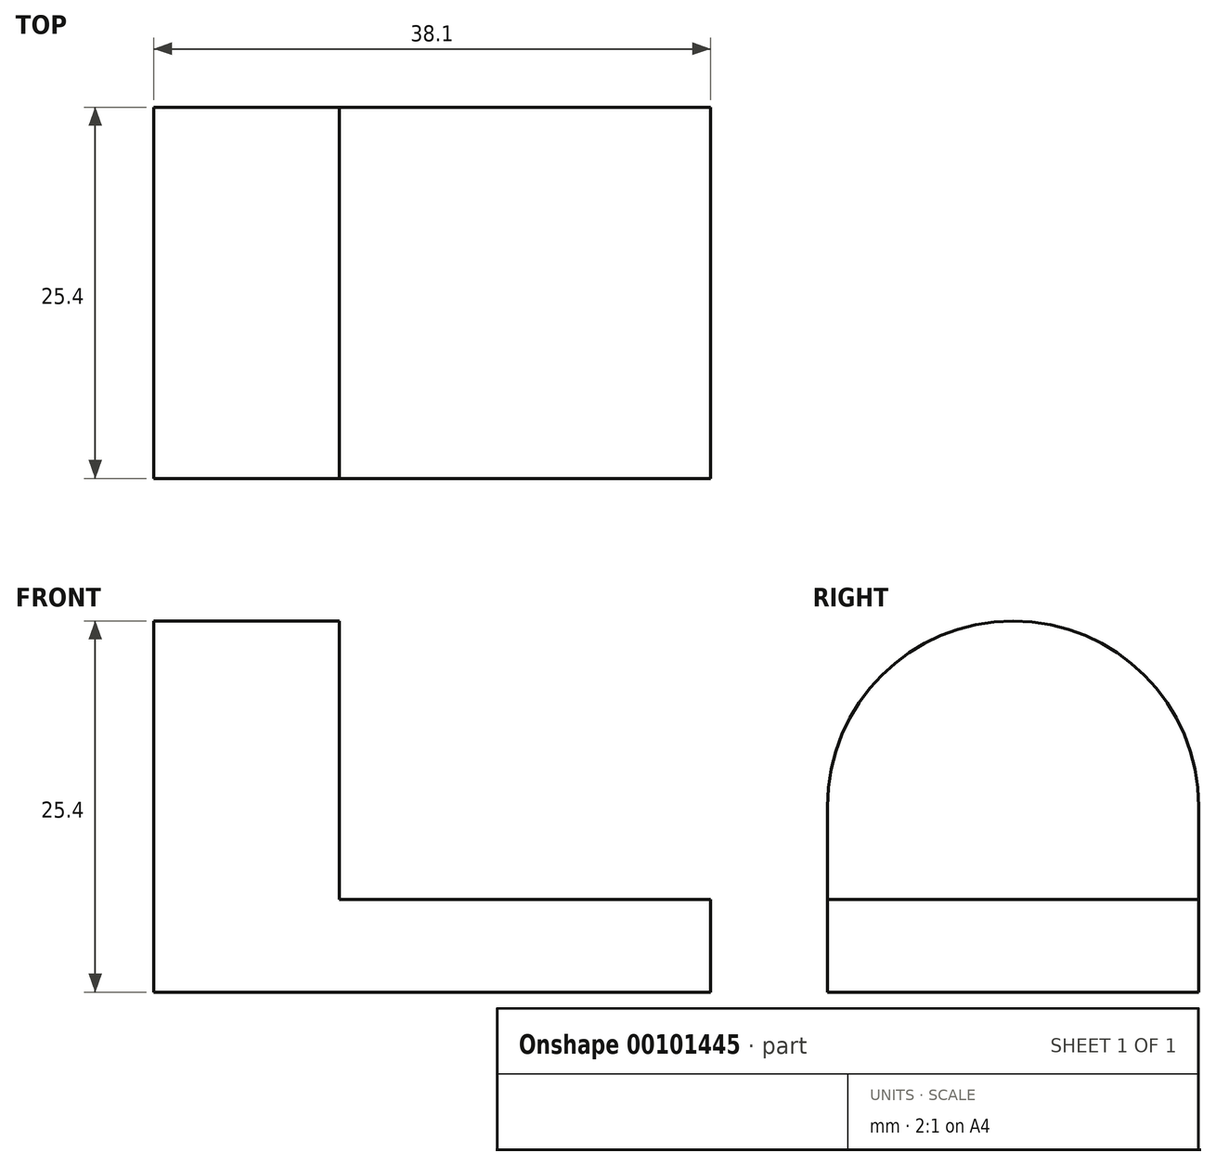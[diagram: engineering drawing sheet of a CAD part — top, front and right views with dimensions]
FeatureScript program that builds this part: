
annotation { "Feature Type Name" : "Feature", "Feature Type Description" : "" }
export const myFeature = defineFeature(function(context is Context, id is Id, definition is map)
    precondition{}
    {
        {
            var Q0;
            Q0=qCreatedBy(makeId("Right.planeOp"),FACE);
            var sketch = newSketch(context, id + "F0", { "sketchPlane" : qUnion([Q0])});
            skLineSegment(sketch, "E0", {"start": v(0, 0) * mm, "end": v(25.4, 0) * mm});
            skLineSegment(sketch, "E1", {"start": v(25.4, 0) * mm, "end": v(25.4, 12.7) * mm});
            skLineSegment(sketch, "E2", {"start": v(0, 0) * mm, "end": v(0, 12.7) * mm});
            skArc(sketch, "E3", {"start": v(25.4, 12.7) * mm, "mid": v(12.7, 25.4) * mm, "end": v(0, 12.7) * mm});
            skSolve(sketch);
        }
        {
            var Q0;
            Q0 = qSketchRegion(id + "F0", true);
            extrude(context, id + "F1", {"entities" : qUnion([Q0]), "depth" : 12.7 * mm});
        }
        {
            var Q0;
            Q0=makeQuery(id+"F1.opExtrude","CAP_FACE",FACE,{"disambiguationData":[OSD([sQuery(id+"F0.wireOp",EDGE,"E0"),sQuery(id+"F0.wireOp",EDGE,"E1"),sQuery(id+"F0.wireOp",EDGE,"E2"),sQuery(id+"F0.wireOp",EDGE,"E3")])],"isStart":false});
            var sketch = newSketch(context, id + "F2", { "sketchPlane" : qUnion([Q0])});
            skLineSegment(sketch, "E4", {"start": v(0, 0) * mm, "end": v(25.4, 0) * mm});
            skLineSegment(sketch, "E5", {"start": v(25.4, 0) * mm, "end": v(25.4, 6.35) * mm});
            skLineSegment(sketch, "E6", {"start": v(25.4, 6.35) * mm, "end": v(0, 6.35) * mm});
            skLineSegment(sketch, "E7", {"start": v(0, 6.35) * mm, "end": v(0, 0) * mm});
            skSolve(sketch);
        }
        {
            var Q0;
            Q0 = qSketchRegion(id + "F2", true);
            extrude(context, id + "F3", {"entities" : qUnion([Q0]), "operationType" : NewBodyOperationType.ADD, "depth" : 25.4 * mm});
        }
    });
